# Revit family: TY-B-TY3251_Metric
name_source: partatom
category: Sprinklers
units: mm (PartAtom-declared; Revit-internal decimal feet)

## family parameters
Always vertical = Yes
Cut with Voids When Loaded = No
Maintain Annotation Orientation = No
OmniClass Number = 23.65.70.17.11.24
OmniClass Title = Fire Fighting Sprinkler Heads
Part Type = Normal
Room Calculation Point = No
Round Connector Dimension = Use Diameter
Shared = No
Work Plane-Based = No

## types (46) — shared parameters
COBie = Yes
COBie.Component.Name = Sprinklers:Pendent_SIN
COBie.Type = Yes
COBie.Type.AssetType = Fixed
COBie.Type.Category = Pr_70_55_97_84:Sprinklers
COBie.Type.Manufacturer = Tyco Fire Protection Products
COBie.Type.Material = Bronze
COBie.Type.Shape = Cylinder
COBie.Type.Size = 1/2"(DN15)
COBie.Type.WarrantyGuarantorParts = http://tycofsbp.com
TFPPTerms_of_Sale.pdf
Coverage = Standard
Coverage_ = Standard
K-Factor = 79.9096
Manufacturer = Tyco Fire Protection Products
Manufacturer URL = www.tyco-fire.com
Material_ = Bronze
Model = TY-B
Nominal Diameter 1 = 15 mm
Orifice = Standard
Orifice Size = 0 mm
Outside Diameter 1 = 21 mm
Response = Standard
Response_ = Standard
SIN No = TY3251
Takeout 1 = 56 mm
Technical Data Sheet No = TFP151
zero-valued in all types: COBie.Type.NominalHeight, COBie.Type.NominalLength, COBie.Type.NominalWidth, COBie.Type.ReplacementCost, Default Elevation, Style Id

## per-type parameters (varying)
| type | COBie.Component.Description | COBie.Type.Colour | COBie.Type.DurationUnit | COBie.Type.Finish | COBie.Type.ModelNumber | COBie.Type.ModelReference | Description | Finish_ | Part No | Temperature Rating |
| Pendent ½" NPT 57°C Brass_57-571-1-135 | TY-B Wet Pendent  135°F K5.6 1/2 NPT Br | Yellow | year | Natural Brass | 57-571-1-135 | TY-B Wet Pendent  135°F K5.6 1/2 NPT Br | TY-B Pendent Brass 57°C 5.6K ½" NPT | Natural Brass | 57-571-1-135 | 57 °C |
| Pendent ½" NPT 68°C Brass_57-571-1-155 | TY-B Wet Pendent  155°F K5.6 1/2 NPT Br | Yellow | year | Natural Brass | 57-571-1-155 | TY-B Wet Pendent  155°F K5.6 1/2 NPT Br | TY-B Pendent Brass 68°C 5.6K ½" NPT | Natural Brass | 57-571-1-155 | 68 °C |
| Pendent ½" NPT 79°C Brass_57-571-1-175 | TY-B Wet Pendent  175°F K5.6 1/2 NPT Br | Yellow | year | Natural Brass | 57-571-1-175 | TY-B Wet Pendent  175°F K5.6 1/2 NPT Br | TY-B Pendent Brass 79°C 5.6K ½" NPT | Natural Brass | 57-571-1-175 | 79 °C |
| Pendent ½" NPT 93°C  Brass_57-571-1-200 | TY-B Wet Pendent  200°F K5.6 1/2 NPT Br | Yellow | year | Natural Brass | 57-571-1-200 | TY-B Wet Pendent  200°F K5.6 1/2 NPT Br | TY-B Pendent Brass 93°C 5.6K ½" NPT | Natural Brass | 57-571-1-200 | 93 °C |
| Pendent ½" NPT 141°C Brass_57-571-1-286 | TY-B Wet Pendent  286°F K5.6 1/2 NPT Br | Yellow | year | Natural Brass | 57-571-1-286 | TY-B Wet Pendent  286°F K5.6 1/2 NPT Br | TY-B Pendent Brass 141°C 5.6K ½" NPT | Natural Brass | 57-571-1-286 | 141 °C |
| Pendent ½" NPT 182°C Brass_57-571-1-360 | TY-B Wet Pendent  360°F K5.6 1/2 NPT Br | Yellow | year | Natural Brass | 57-571-1-360 | TY-B Wet Pendent  360°F K5.6 1/2 NPT Br | TY-B Pendent Brass 182°C 5.6K ½" NPT | Natural Brass | 57-571-1-360 | 182 °C |
| Pendent ½" NPT 57°C Gray_57-571-2-135 | TY-B Wet Pendent  135°F K5.6 1/2 NPT RAL9007 | Gray | year | Poly-Stainless Gray | 57-571-2-135 | TY-B Wet Pendent  135°F K5.6 1/2 NPT RAL9007 | TY-B Pendent Brass 57°C 5.6K ½" NPT | Poly Stainless Steel Gray Aluminium Polyester | 57-571-2-135 | 57 °C |
| Pendent ½" NPT 68°C Gray_57-571-2-155 | TY-B Wet Pendent  155°F K5.6 1/2 NPT RAL9007 | Gray | year | Poly-Stainless Gray | 57-571-2-155 | TY-B Wet Pendent  155°F K5.6 1/2 NPT RAL9007 | TY-B Pendent Brass 68°C 5.6K ½" NPT | Poly Stainless Steel Gray Aluminium Polyester | 57-571-2-155 | 68 °C |
| Pendent ½" NPT 79°C Gray_57-571-2-175 | TY-B Wet Pendent  175°F K5.6 1/2 NPT RAL9007 | Gray | year | Poly-Stainless Gray | 57-571-2-175 | TY-B Wet Pendent  175°F K5.6 1/2 NPT RAL9007 | TY-B Pendent Brass 79°C 5.6K ½" NPT | Poly Stainless Steel Gray Aluminium Polyester | 57-571-2-175 | 79 °C |
| Pendent ½" NPT 93°C Gray_57-571-2-200 | TY-B Wet Pendent  200°F K5.6 1/2 NPT RAL9007 | Gray | year | Poly-Stainless Gray | 57-571-2-200 | TY-B Wet Pendent  200°F K5.6 1/2 NPT RAL9007 | TY-B Pendent Brass 93°C 5.6K ½" NPT | Poly Stainless Steel Gray Aluminium Polyester | 57-571-2-200 | 93 °C |
| Pendent ½" NPT 141°C Gray_57-571-2-286 | TY-B Wet Pendent  286°F K5.6 1/2 NPT RAL9007 | Gray | year | Poly-Stainless Gray | 57-571-2-286 | TY-B Wet Pendent  286°F K5.6 1/2 NPT RAL9007 | TY-B Pendent Brass 141°C 5.6K ½" NPT | Poly Stainless Steel Gray Aluminium Polyester | 57-571-2-286 | 141 °C |
| Pendent ½" NPT 182°C Gray_57-571-2-360 | TY-B Wet Pendent  360°F K5.6 1/2 NPT RAL9007 | Gray | year | Poly-Stainless Gray | 57-571-2-360 | TY-B Wet Pendent  360°F K5.6 1/2 NPT RAL9007 | TY-B Pendent Brass 182°C 5.6K ½" NPT | Poly Stainless Steel Gray Aluminium Polyester | 57-571-2-360 | 182 °C |
| Pendent ½" NPT 57°C White_57-571-3-135 | TY-B Wet Pendent  135°F K5.6 1/2 NPT Wh9010 | White | year | Pure White | 57-571-3-135 | TY-B Wet Pendent  135°F K5.6 1/2 NPT Wh9010 | TY-B Pendent White 57°C 5.6K ½" NPT | White RAL9010 | 57-571-3-135 | 57 °C |
| Pendent ½" NPT 68°C White_57-571-3-155 | TY-B Wet Pendent  155°F K5.6 1/2 NPT Wh9010 | White | year | Pure White | 57-571-3-155 | TY-B Wet Pendent  155°F K5.6 1/2 NPT Wh9010 | TY-B Pendent White 68°C 5.6K ½" NPT | White RAL9010 | 57-571-3-155 | 68 °C |
| Pendent ½" NPT 79°C White_57-571-3-175 | TY-B Wet Pendent  175°F K5.6 1/2 NPT Wh9010 | White | year | Pure White | 57-571-3-175 | TY-B Wet Pendent  175°F K5.6 1/2 NPT Wh9010 | TY-B Pendent White 79°C 5.6K ½" NPT | White RAL9010 | 57-571-3-175 | 79 °C |
| Pendent ½" NPT 93°C White_57-571-3-200 | TY-B Wet Pendent  200°F K5.6 1/2 NPT Wh9010 | White | year | Pure White | 57-571-3-200 | TY-B Wet Pendent  200°F K5.6 1/2 NPT Wh9010 | TY-B Pendent White 93°C 5.6K ½" NPT | White RAL9010 | 57-571-3-200 | 93 °C |
| Pendent ½" NPT 141°C White_57-571-3-286 | TY-B Wet Pendent  286°F K5.6 1/2 NPT Wh9010 | White | year | Pure White | 57-571-3-286 | TY-B Wet Pendent  286°F K5.6 1/2 NPT Wh9010 | TY-B Pendent White 141°C 5.6K ½" NPT | White RAL9010 | 57-571-3-286 | 141 °C |
| Pendent ½" NPT 182°C White_57-571-3-360 | TY-B Wet Pendent  360°F K5.6 1/2 NPT Wh9010 | White | year | Pure White | 57-571-3-360 | TY-B Wet Pendent  360°F K5.6 1/2 NPT Wh9010 | TY-B Pendent White 182°C 5.6K ½" NPT | White RAL9010 | 57-571-3-360 | 182 °C |
| Pendent ½" NPT 57°C White_57-571-4-135 | TY-B Wet Pendent  135°F K5.6 1/2 NPT Wh9003 | White | year | Signal White | 57-571-4-135 | TY-B Wet Pendent  135°F K5.6 1/2 NPT Wh9003 | TY-B Pendent White 57°C 5.6K ½" NPT | White RAL9003 | 57-571-4-135 | 57 °C |
| Pendent ½" NPT 68°C White_57-571-4-155 | TY-B Wet Pendent  155°F K5.6 1/2 NPT Wh9003 | White | year | Signal White | 57-571-4-155 | TY-B Wet Pendent  155°F K5.6 1/2 NPT Wh9003 | TY-B Pendent White 68°C 5.6K ½" NPT | White RAL9003 | 57-571-4-155 | 68 °C |
| Pendent ½" NPT 79°C White_57-571-4-175 | TY-B Wet Pendent  175°F K5.6 1/2 NPT Wh9003 | White | Year | Signal White | 57-571-4-175 | TY-B Wet Pendent  175°F K5.6 1/2 NPT Wh9003 | TY-B Pendent White 79°C 5.6K ½" NPT | White RAL9003 | 57-571-4-175 | 79 °C |
| Pendent ½" NPT 93°C White_57-571-4-200 | TY-B Wet Pendent  200°F K5.6 1/2 NPT Wh9003 | White | year | Signal White | 57-571-4-200 | TY-B Wet Pendent  200°F K5.6 1/2 NPT Wh9003 | TY-B Pendent White 93°C 5.6K ½" NPT | White RAL9003 | 57-571-4-200 | 93 °C |
| Pendent ½" NPT 141°C White_57-571-4-286 | TY-B Wet Pendent  286°F K5.6 1/2 NPT Wh9003 | White | year | Signal White | 57-571-4-286 | TY-B Wet Pendent  286°F K5.6 1/2 NPT Wh9003 | TY-B Pendent White 141°C 5.6K ½" NPT | White RAL9003 | 57-571-4-286 | 141 °C |
| Pendent ½" NPT 182°C White_57-571-4-360 | TY-B Wet Pendent  360°F K5.6 1/2 NPT Wh9003 | White | year | Signal White | 57-571-4-360 | TY-B Wet Pendent  360°F K5.6 1/2 NPT Wh9003 | TY-B Pendent White 182°C 5.6K ½" NPT | White RAL9003 | 57-571-4-360 | 182 °C |
| Pendent ½" NPT 57°C Wax_57-571-6-135 | TY-B Wet Pendent  135°F K5.6 1/2 NPT Wx | Gray | year | Wax Coated | 57-571-6-135 | TY-B Wet Pendent  135°F K5.6 1/2 NPT Wx | TY-B Pendent Wax 57°C 5.6K ½" NPT | Wax Coated | 57-571-6-135 | 57 °C |
| Pendent ½" NPT 68°C Wax_57-571-6-155 | TY-B Wet Pendent  155°F K5.6 1/2 NPT Wx | Gray | year | Wax Coated | 57-571-6-155 | TY-B Wet Pendent  155°F K5.6 1/2 NPT Wx | TY-B Pendent Wax 68°C 5.6K ½" NPT | Wax Coated | 57-571-6-155 | 68 °C |
| Pendent ½" NPT 79°C Wax_57-571-6-175 | TY-B Wet Pendent  175°F K5.6 1/2 NPT Wx | Gray | year | Wax Coated | 57-571-6-175 | TY-B Wet Pendent  175°F K5.6 1/2 NPT Wx | TY-B Pendent Wax 79°C 5.6K ½" NPT | Wax Coated | 57-571-6-175 | 79 °C |
| Pendent ½" NPT 93°C Wax_57-571-6-200 | TY-B Wet Pendent  200°F K5.6 1/2 NPT Wx | Gray | year | Wax Coated | 57-571-6-200 | TY-B Wet Pendent  200°F K5.6 1/2 NPT Wx | TY-B Pendent Wax 93°C 5.6K ½" NPT | Wax Coated | 57-571-6-200 | 93 °C |
| Pendent ½" NPT 141°C Wax_57-571-6-286 | TY-B Wet Pendent  286°F K5.6 1/2 NPT Wx | Gray | year | Wax Coated | 57-571-6-286 | TY-B Wet Pendent  286°F K5.6 1/2 NPT Wx | TY-B Pendent Wax 141°C 5.6K ½" NPT | Wax Coated | 57-571-6-286 | 141 °C |
| Pendent ½" NPT 57°C Lead_57-571-7-135 | TY-B Wet Pendent  135°F K5.6 1/2 NPT Lead | Gray | year | Lead Coated | 57-571-7-135 | TY-B Wet Pendent  135°F K5.6 1/2 NPT Lead | TY-B Pendent Lead 57°C 5.6K ½" NPT | Lead Coated | 57-571-7-135 | 57 °C |
| Pendent ½" NPT 68°C Lead_57-571-7-155 | TY-B Wet Pendent  155°F K5.6 1/2 NPT Lead | Gray | year | Lead Coated | 57-571-7-155 | TY-B Wet Pendent  155°F K5.6 1/2 NPT Lead | TY-B Pendent Lead 68°C 5.6K ½" NPT | Lead Coated | 57-571-7-155 | 68 °C |
| Pendent ½" NPT 79°C Lead_57-571-7-175 | TY-B Wet Pendent  175°F K5.6 1/2 NPT Lead | Gray | year | Leqad Coated | 57-571-7-175 | TY-B Wet Pendent  175°F K5.6 1/2 NPT Lead | TY-B Pendent Lead 79°C 5.6K ½" NPT | Lead Coated | 57-571-7-175 | 79 °C |
| Pendent ½" NPT 93°C Lead_57-571-7-200 | TY-B Wet Pendent  200°F K5.6 1/2 NPT Lead | Gray | year | Lead Coated | 57-571-7-200 | TY-B Wet Pendent  200°F K5.6 1/2 NPT Lead | TY-B Pendent Lead 93°C 5.6K ½" NPT | Lead Coated | 57-571-7-200 | 93 °C |
| Pendent ½" NPT 141°C Lead_57-571-7-286 | TY-B Wet Pendent  286°F K5.6 1/2 NPT Lead | Gray | year | Lead Coated | 57-571-7-286 | TY-B Wet Pendent  286°F K5.6 1/2 NPT Lead | TY-B Pendent Lead 141°C 5.6K ½" NPT | Lead Coated | 57-571-7-286 | 141 °C |
| Pendent ½" NPT 182°C Lead_57-571-7-360 | TY-B Wet Pendent  360°F K5.6 1/2 NPT Lead | Gray | year | Lead Coated | 57-571-7-360 | TY-B Wet Pendent  360°F K5.6 1/2 NPT Lead | TY-B Pendent Lead 182°C 5.6K ½" NPT | Lead Coated | 57-571-7-360 | 182 °C |
| Pendent ½" NPT 57°C Wax Over Lead_57-571-8-135 | TY-B Wet Pendent  135°F K5.6 1/2 NPT WoL | Gray | year | Wax-Over-Lead | 57-571-8-135 | TY-B Wet Pendent  135°F K5.6 1/2 NPT WoL | TY-B Pendent Wax Over Lead 57°C 5.6K ½" NPT | Wax Over Lead | 57-571-8-135 | 57 °C |
| Pendent ½" NPT 68°C Wax over Lead_57-571-8-155 | TY-B Wet Pendent  155°F K5.6 1/2 NPT WoL | Gray | year | Wax-Over-Lead | 57-571-8-155 | TY-B Wet Pendent  155°F K5.6 1/2 NPT WoL | TY-B Pendent Wax Over Lead 68°C 5.6K ½" NPT | Wax Over Lead | 57-571-8-155 | 68 °C |
| Pendent ½" NPT 79°C Wax Over Lead_57-571-8-175 | TY-B Wet Pendent  175°F K5.6 1/2 NPT WoL | Gray | year | Wax-Over-Lead | 57-571-8-175 | TY-B Wet Pendent  175°F K5.6 1/2 NPT WoL | TY-B Pendent Wax Over Lead 79°C 5.6K ½" NPT | Wax Over Lead | 57-571-8-175 | 79 °C |
| Pendent ½" NPT 93°C Wax Over Lead_57-571-8-200 | TY-B Wet Pendent  200°F K5.6 1/2 NPT WoL | Gray | year | Wax-Over-Lead | 57-571-8-200 | TY-B Wet Pendent  200°F K5.6 1/2 NPT WoL | TY-B Pendent Wax Over Lead 93°C 5.6K ½" NPT | Wax Over Lead | 57-571-8-200 | 93 °C |
| Pendent ½" NPT 141°C Wax Over Lead_57-571-8-286 | TY-B Wet Pendent  286°F K5.6 1/2 NPT WoL | Gray | year | Wax-Over-Lead | 57-571-8-286 | TY-B Wet Pendent  286°F K5.6 1/2 NPT WoL | TY-B Pendent Wax Over Lead 141°C 5.6K ½" NPT | Wax Over Lead | 57-571-8-286 | 141 °C |
| Pendent ½" NPT 57°C Chrome_57-571-9-135 | TY-B Wet Pendent  135°F K5.6 1/2 NPT Chr | Silver | year | Chrome Plated | 57-571-9-135 | TY-B Wet Pendent  135°F K5.6 1/2 NPT Chr | TY-B Pendent Chrome 57°C 5.6K ½" NPT | Chrome Plated | 57-571-9-135 | 57 °C |
| Pendent ½" NPT 68°C Chrome_57-571-9-155 | TY-B Wet Pendent  155°F K5.6 1/2 NPT Chr | Silver | year | Chrome Plated | 57-571-9-155 | TY-B Wet Pendent  155°F K5.6 1/2 NPT Chr | TY-B Pendent Chrome 68°C 5.6K ½" NPT | Chrome Plated | 57-571-9-155 | 68 °C |
| Pendent ½" NPT 79°C Chrome_57-571-9-175 | TY-B Wet Pendent  175°F K5.6 1/2 NPT Chr | Silver | year | Chrome Plated | 57-571-9-175 | TY-B Wet Pendent  175°F K5.6 1/2 NPT Chr | TY-B Pendent Chrome 79°C 5.6K ½" NPT | Chrome Plated | 57-571-9-175 | 79 °C |
| Pendent ½" NPT 93°C Chrome_57-571-9-200 | TY-B Wet Pendent  200°F K5.6 1/2 NPT Chr | Silver | year | Chrome Plated | 57-571-9-200 | TY-B Wet Pendent  200°F K5.6 1/2 NPT Chr | TY-B Pendent Chrome 93°C 5.6K ½" NPT | Chrome Plated | 57-571-9-200 | 93 °C |
| Pendent ½" NPT 141°C Chrome_57-571-9-286 | TY-B Wet Pendent  286°F K5.6 1/2 NPT Chr | Silver | year | Chrome Plated | 57-571-9-286 | TY-B Wet Pendent  286°F K5.6 1/2 NPT Chr | TY-B Pendent Chrome 141°C 5.6K ½" NPT | Chrome Plated | 57-571-9-286 | 141 °C |
| Pendent ½" NPT 182°C Chrome_57-571-9-360 | TY-B Wet Pendent  360°F K5.6 1/2 NPT Chr | Silver | year | Chrome Plated | 57-571-9-360 | TY-B Wet Pendent  360°F K5.6 1/2 NPT Chr | TY-B Pendent Chrome 182°C 5.6K ½" NPT | Chrome Plated | 57-571-9-360 | 182 °C |

## geometry (parser evidence)
native form markers: Blend x2, Sweep x52
no freeform markers — native parametric forms only
